# Revit family: Table-LAMMHULTS-QUICKLY-Std_Leg
name_source: partatom
category: Furniture
revit_build: Autodesk Revit Architecture 2012 (Build: 20110916_2132(x64)
units: mm (PartAtom-declared; Revit-internal decimal feet)

## types (1)
- Table-LAMMHULTS-QUICKLY-Std_Leg
    Assembly Code = E2020
    Description = *Please enter mtrl description here for use in mto*
    Frame Distance = 160 mm  [stored 0.524934 ft]
    Keynote = 46.B
    Legs Material = Metal - Chrome - Polished
    Manufacturer = LAMMHULTS
    Model = *Furniture model*
    Table Edge Material = Wood - Veneer - Birch
    Table Top Length = 1400 mm  [stored 4.59318 ft]
    Table Top Material = Wood - Veneer - Birch
    Table Top Width = 600 mm
    URL = www.lammhults.se
    _Leg Width = 470 mm  [stored 1.54199 ft]

note: [stored X ft] marks values corroborated as IEEE doubles in the binary element streams (Revit-internal decimal feet)

## geometry (parser evidence)
native form markers: Blend x12, Sweep x1
no freeform markers — native parametric forms only
